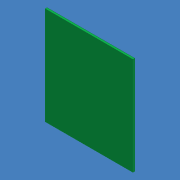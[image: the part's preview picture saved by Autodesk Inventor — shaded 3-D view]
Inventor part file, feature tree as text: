
AUTODESK INVENTOR PART (.ipt)
format: ipt  version: unknown  size: 167,424 bytes
history: native  units: mm (DEFAULTED — no unit token found)
features: extrude x1, sketch x1
ambient origin geometry x8: Origin, YZ Plane, XZ Plane, XY Plane, X Axis, Y Axis, Z Axis, Center Point
feature tree (2):
  extrude  "Extrusion1"  Depth=73.66mm
  sketch  "Sketch1"  dims[d0=66.04mm d1=73.66mm d2=1.4224mm d3=0.0mm]
